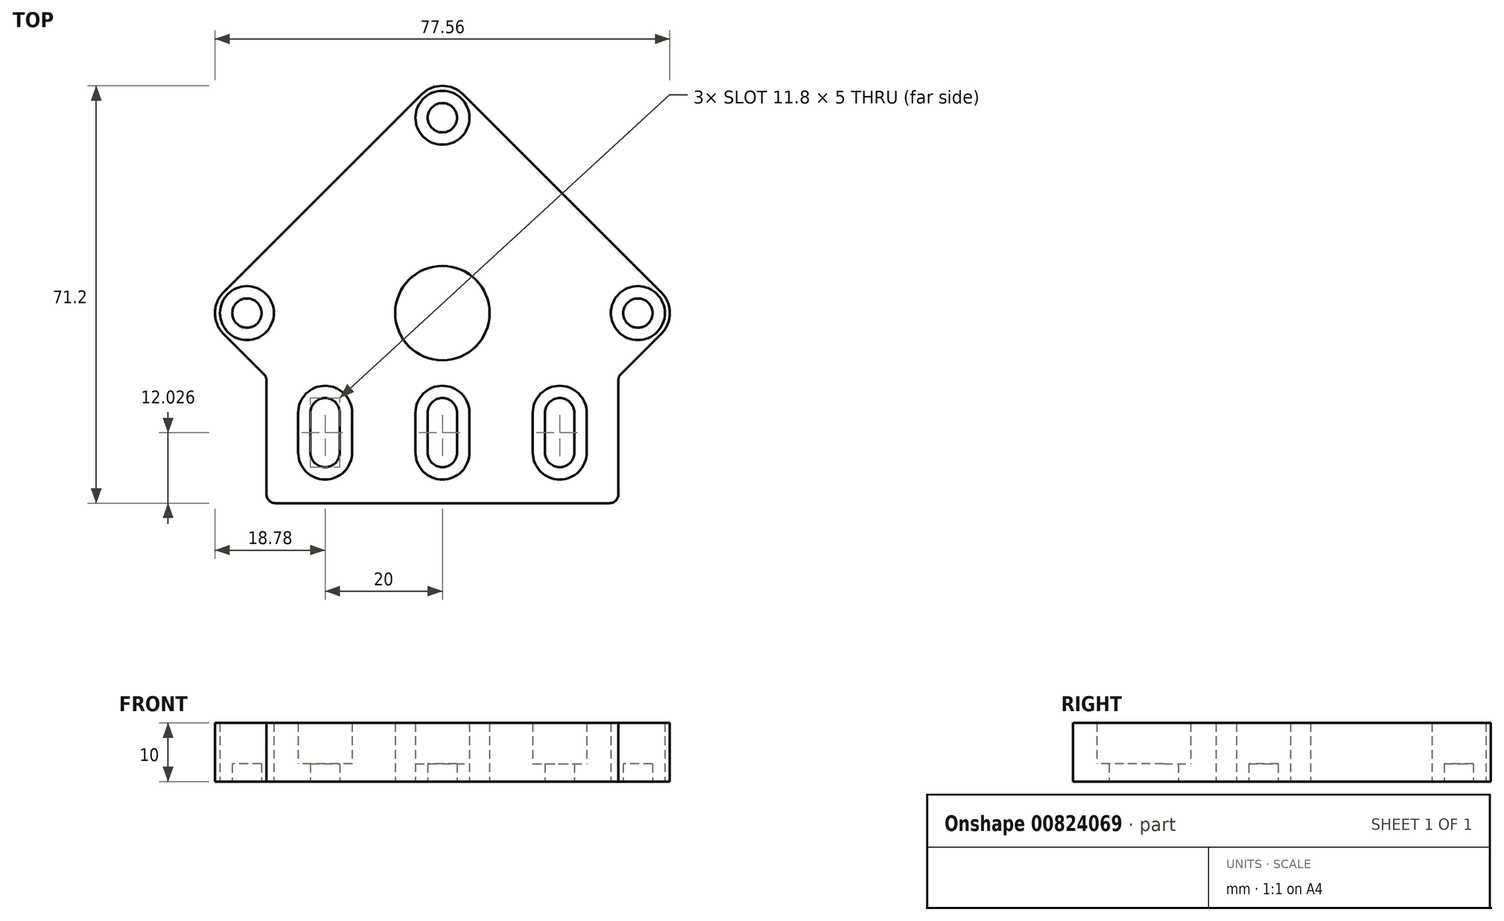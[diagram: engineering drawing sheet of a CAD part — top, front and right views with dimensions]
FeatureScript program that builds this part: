
annotation { "Feature Type Name" : "Feature", "Feature Type Description" : "" }
export const myFeature = defineFeature(function(context is Context, id is Id, definition is map)
    precondition{}
    {
        {
            var Q0;
            Q0=qCreatedBy(makeId("Top.planeOp"),FACE);
            var sketch = newSketch(context, id + "F0", { "sketchPlane" : qUnion([Q0])});
            skLineSegment(sketch, "E0", {"start": v(-28.5, -35.6) * mm, "end": v(28.5, -35.6) * mm});
            skLineSegment(sketch, "E1", {"start": v(-37.31, -6.7) * mm, "end": v(-30.44, -13.58) * mm});
            skLineSegment(sketch, "E2", {"start": v(-30, -14.65) * mm, "end": v(-30, -34.1) * mm});
            skLineSegment(sketch, "E3", {"start": v(-3.54, 34.14) * mm, "end": v(-37.31, 0.36) * mm});
            skLineSegment(sketch, "E4", {"start": v(-22.5, -26.97) * mm, "end": v(-22.5, -20.17) * mm});
            skLineSegment(sketch, "E5", {"start": v(-17.5, -20.17) * mm, "end": v(-17.5, -26.97) * mm});
            skLineSegment(sketch, "E6", {"start": v(-2.5, -26.97) * mm, "end": v(-2.5, -20.17) * mm});
            skLineSegment(sketch, "E7", {"start": v(2.5, -20.17) * mm, "end": v(2.5, -26.97) * mm});
            skLineSegment(sketch, "E8", {"start": v(17.5, -26.97) * mm, "end": v(17.5, -20.17) * mm});
            skLineSegment(sketch, "E9", {"start": v(22.5, -20.17) * mm, "end": v(22.5, -26.97) * mm});
            skLineSegment(sketch, "E10", {"start": v(37.31, 0.36) * mm, "end": v(3.54, 34.14) * mm});
            skLineSegment(sketch, "E11", {"start": v(30, -34.1) * mm, "end": v(30, -14.65) * mm});
            skLineSegment(sketch, "E12", {"start": v(30.44, -13.58) * mm, "end": v(37.31, -6.7) * mm});
            skCircle(sketch, "E13", {"center": v(0, -3.17) * mm, "radius": 8.05 * mm});
            skCircle(sketch, "E14", {"center": v(0, -3.17) * mm, "radius": 5.5 * mm});
            skArc(sketch, "E15", {"start": v(37.31, -6.7) * mm, "mid": v(38.78, -3.17) * mm, "end": v(37.31, 0.36) * mm});
            skArc(sketch, "E16", {"start": v(3.54, 34.14) * mm, "mid": v(0, 35.6) * mm, "end": v(-3.54, 34.14) * mm});
            skArc(sketch, "E17", {"start": v(-37.31, 0.36) * mm, "mid": v(-38.78, -3.17) * mm, "end": v(-37.31, -6.7) * mm});
            skCircle(sketch, "E18", {"center": v(0, 30.16) * mm, "radius": 2.5 * mm});
            skCircle(sketch, "E19", {"center": v(33.33, -3.17) * mm, "radius": 2.5 * mm});
            skCircle(sketch, "E20", {"center": v(-33.33, -3.17) * mm, "radius": 2.5 * mm});
            skArc(sketch, "E21", {"start": v(17.5, -26.97) * mm, "mid": v(20, -29.47) * mm, "end": v(22.5, -26.97) * mm});
            skArc(sketch, "E22", {"start": v(22.5, -20.17) * mm, "mid": v(20, -17.67) * mm, "end": v(17.5, -20.17) * mm});
            skArc(sketch, "E23", {"start": v(-2.5, -26.97) * mm, "mid": v(0, -29.47) * mm, "end": v(2.5, -26.97) * mm});
            skArc(sketch, "E24", {"start": v(2.5, -20.17) * mm, "mid": v(0, -17.67) * mm, "end": v(-2.5, -20.17) * mm});
            skArc(sketch, "E25", {"start": v(-22.5, -26.97) * mm, "mid": v(-20, -29.47) * mm, "end": v(-17.5, -26.97) * mm});
            skArc(sketch, "E26", {"start": v(-17.5, -20.17) * mm, "mid": v(-20, -17.67) * mm, "end": v(-22.5, -20.17) * mm});
            skArc(sketch, "E27", {"start": v(28.5, -35.6) * mm, "mid": v(29.56, -35.16) * mm, "end": v(30, -34.1) * mm});
            skArc(sketch, "E28", {"start": v(30.44, -13.58) * mm, "mid": v(30.11, -14.07) * mm, "end": v(30, -14.65) * mm});
            skArc(sketch, "E29", {"start": v(-30, -14.65) * mm, "mid": v(-30.11, -14.07) * mm, "end": v(-30.44, -13.58) * mm});
            skArc(sketch, "E30", {"start": v(-30, -34.1) * mm, "mid": v(-29.56, -35.16) * mm, "end": v(-28.5, -35.6) * mm});
            skCircle(sketch, "E31.0", {"center": v(-33.33, -3.17) * mm, "radius": 4.6 * mm});
            skArc(sketch, "E32.0", {"start": v(-15.4, -20.17) * mm, "mid": v(-20, -15.57) * mm, "end": v(-24.6, -20.17) * mm});
            skLineSegment(sketch, "E32.1", {"start": v(-15.4, -20.17) * mm, "end": v(-15.4, -26.97) * mm});
            skArc(sketch, "E32.2", {"start": v(-24.6, -26.97) * mm, "mid": v(-20, -31.57) * mm, "end": v(-15.4, -26.97) * mm});
            skLineSegment(sketch, "E32.3", {"start": v(-24.6, -26.97) * mm, "end": v(-24.6, -20.17) * mm});
            skLineSegment(sketch, "E33.0", {"start": v(-4.6, -26.97) * mm, "end": v(-4.6, -20.17) * mm});
            skArc(sketch, "E33.1", {"start": v(-4.6, -26.97) * mm, "mid": v(0, -31.57) * mm, "end": v(4.6, -26.97) * mm});
            skLineSegment(sketch, "E33.2", {"start": v(4.6, -20.17) * mm, "end": v(4.6, -26.97) * mm});
            skArc(sketch, "E33.3", {"start": v(4.6, -20.17) * mm, "mid": v(0, -15.57) * mm, "end": v(-4.6, -20.17) * mm});
            skLineSegment(sketch, "E34.0", {"start": v(15.4, -26.97) * mm, "end": v(15.4, -20.17) * mm});
            skArc(sketch, "E34.1", {"start": v(15.4, -26.97) * mm, "mid": v(20, -31.57) * mm, "end": v(24.6, -26.97) * mm});
            skLineSegment(sketch, "E34.2", {"start": v(24.6, -20.17) * mm, "end": v(24.6, -26.97) * mm});
            skArc(sketch, "E34.3", {"start": v(24.6, -20.17) * mm, "mid": v(20, -15.57) * mm, "end": v(15.4, -20.17) * mm});
            skCircle(sketch, "E35.0", {"center": v(33.33, -3.17) * mm, "radius": 4.6 * mm});
            skCircle(sketch, "E36.0", {"center": v(0, 30.16) * mm, "radius": 4.6 * mm});
            skSolve(sketch);
        }
        {
            var Q0;
            Q0=qSketchRegion(id+"F0",true);
            extrude(context, id + "F1", {"entities" : qUnion([Q0]), "depth" : 10 * mm, "offsetDistance" : 25 * mm});
        }
        {
            var Q0;
            Q0=makeQuery(id+"F0.imprint","IMPRINT",FACE,{"disambiguationData":[TD([[makeQuery(id+"F0.imprint","IMPRINT",EDGE,{"derivedFrom":sQuery(id+"F0.wireOp",EDGE,"E20")}),1.0]])]});
            var Q1;
            Q1=makeQuery(id+"F0.imprint","IMPRINT",FACE,{"disambiguationData":[TD([[makeQuery(id+"F0.imprint","IMPRINT",EDGE,{"derivedFrom":sQuery(id+"F0.wireOp",EDGE,"E4")}),1.0]])]});
            var Q2;
            Q2=makeQuery(id+"F0.imprint","IMPRINT",FACE,{"disambiguationData":[TD([[makeQuery(id+"F0.imprint","IMPRINT",EDGE,{"derivedFrom":sQuery(id+"F0.wireOp",EDGE,"E6")}),1.0]])]});
            var Q3;
            Q3=makeQuery(id+"F0.imprint","IMPRINT",FACE,{"disambiguationData":[TD([[makeQuery(id+"F0.imprint","IMPRINT",EDGE,{"derivedFrom":sQuery(id+"F0.wireOp",EDGE,"E8")}),1.0]])]});
            var Q4;
            Q4=makeQuery(id+"F0.imprint","IMPRINT",FACE,{"disambiguationData":[TD([[makeQuery(id+"F0.imprint","IMPRINT",EDGE,{"derivedFrom":sQuery(id+"F0.wireOp",EDGE,"E19")}),1.0]])]});
            var Q5;
            Q5=makeQuery(id+"F0.imprint","IMPRINT",FACE,{"disambiguationData":[TD([[makeQuery(id+"F0.imprint","IMPRINT",EDGE,{"derivedFrom":sQuery(id+"F0.wireOp",EDGE,"E18")}),1.0]])]});
            extrude(context, id + "F2", {"entities" : qUnion([Q0, Q1, Q2, Q3, Q4, Q5]), "operationType" : NewBodyOperationType.ADD, "depth" : 3 * mm, "offsetDistance" : 25 * mm});
        }
    });
